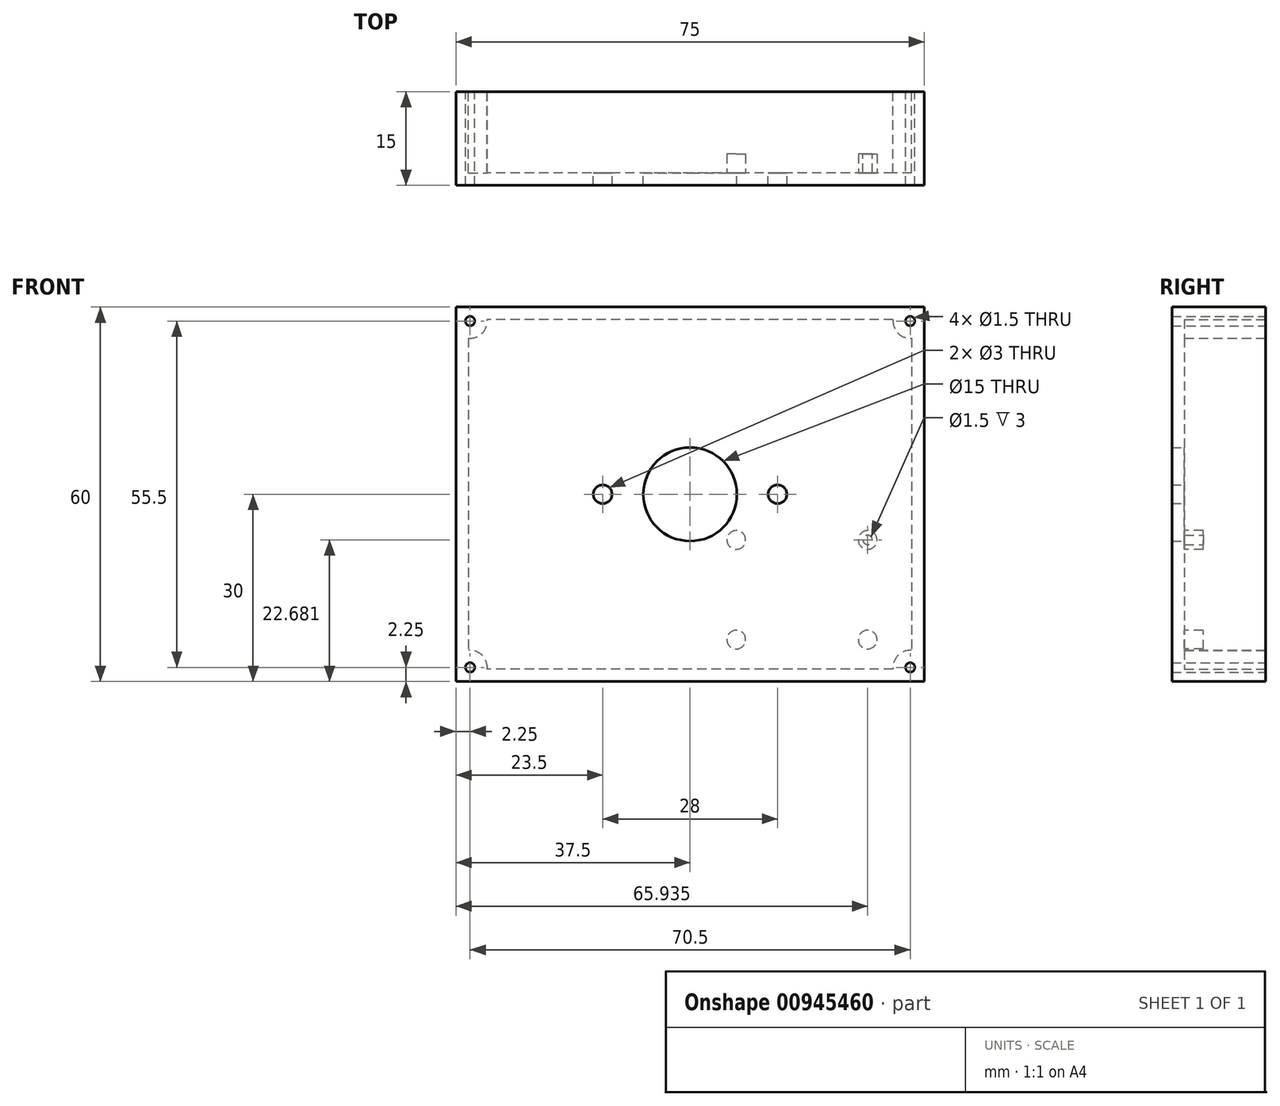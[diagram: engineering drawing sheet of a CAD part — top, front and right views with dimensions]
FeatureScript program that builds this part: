
annotation { "Feature Type Name" : "Feature", "Feature Type Description" : "" }
export const myFeature = defineFeature(function(context is Context, id is Id, definition is map)
    precondition{}
    {
        {
            var Q0;
            Q0=qCreatedBy(makeId("Front.planeOp"),FACE);
            var sketch = newSketch(context, id + "F0", { "sketchPlane" : qUnion([Q0])});
            skLineSegment(sketch, "E0.bottom", {"start": v(37.5, 30) * mm, "end": v(-37.5, 30) * mm});
            skLineSegment(sketch, "E0.top", {"start": v(37.5, -30) * mm, "end": v(-37.5, -30) * mm});
            skLineSegment(sketch, "E0.left", {"start": v(37.5, 30) * mm, "end": v(37.5, -30) * mm});
            skPoint(sketch, "E0.middle", {"position": v(0, 0) * mm});
            skCircle(sketch, "E1", {"center": v(0, 0) * mm, "radius": 7.5 * mm});
            skCircle(sketch, "E2", {"center": v(14, 0) * mm, "radius": 1.5 * mm});
            skCircle(sketch, "E3", {"center": v(-14, 0) * mm, "radius": 1.5 * mm});
            skLineSegment(sketch, "E4.left", {"start": v(-37.5, 30) * mm, "end": v(-37.5, -30) * mm});
            skCircle(sketch, "E5", {"center": v(-35.25, 27.75) * mm, "radius": 0.75 * mm});
            skCircle(sketch, "E6", {"center": v(35.25, 27.75) * mm, "radius": 0.75 * mm});
            skCircle(sketch, "E7", {"center": v(35.25, -27.75) * mm, "radius": 0.75 * mm});
            skCircle(sketch, "E8", {"center": v(-35.25, -27.75) * mm, "radius": 0.75 * mm});
            skSolve(sketch);
        }
        {
            var Q0;
            Q0=qSketchRegion(id+"F0",true);
            var Q1;
            Q1=makeQuery(id+"F0.imprint","IMPRINT",FACE,{"disambiguationData":[TD([[makeQuery(id+"F0.imprint","IMPRINT",EDGE,{"derivedFrom":sQuery(id+"F0.wireOp",EDGE,"E3")}),1.0]])]});
            var Q2;
            Q2=makeQuery(id+"F0.imprint","IMPRINT",FACE,{"disambiguationData":[TD([[makeQuery(id+"F0.imprint","IMPRINT",EDGE,{"derivedFrom":sQuery(id+"F0.wireOp",EDGE,"E1")}),1.0]])]});
            var Q3;
            Q3=makeQuery(id+"F0.imprint","IMPRINT",FACE,{"disambiguationData":[TD([[makeQuery(id+"F0.imprint","IMPRINT",EDGE,{"derivedFrom":sQuery(id+"F0.wireOp",EDGE,"E2")}),1.0]])]});
            extrude(context, id + "F1", {"entities" : qUnion([Q0, Q1, Q2, Q3]), "endBound" : BoundingType.SYMMETRIC, "depth" : 15 * mm, "offsetDistance" : 25.4 * mm});
        }
        {
            var Q0;
            Q0=makeQuery(id+"F1.opExtrude","CAP_FACE",FACE,{"disambiguationData":[OSD([sQuery(id+"F0.wireOp",EDGE,"E0.top"),sQuery(id+"F0.wireOp",EDGE,"E0.left"),sQuery(id+"F0.wireOp",EDGE,"E1"),sQuery(id+"F0.wireOp",EDGE,"E2"),sQuery(id+"F0.wireOp",EDGE,"E3"),sQuery(id+"F0.wireOp",EDGE,"E4.bottom"),sQuery(id+"F0.wireOp",EDGE,"E4.left"),sQuery(id+"F0.wireOp",EDGE,"054ACI62-jY1l-R8Cq-kHqT-064Rme7hxepK.bottom"),sQuery(id+"F0.wireOp",EDGE,"054ACI62-jY1l-R8Cq-kHqT-064Rme7hxepK.right"),sQuery(id+"F0.wireOp",EDGE,"E5"),sQuery(id+"F0.wireOp",EDGE,"E6"),sQuery(id+"F0.wireOp",EDGE,"8eQuBZQc-js6f-clw7-0T8J-KEzLaIp8Z2mv.bottom"),sQuery(id+"F0.wireOp",EDGE,"8eQuBZQc-js6f-clw7-0T8J-KEzLaIp8Z2mv.left"),sQuery(id+"F0.wireOp",EDGE,"E7"),sQuery(id+"F0.wireOp",EDGE,"E8")])],"isStart":true});
            shell(context, id + "F2", {"entities" : qUnion([Q0]), "thickness" : 2 * mm});
        }
        {
            var Q0;
            Q0=makeQuery(id+"F0.imprint","IMPRINT",FACE,{"disambiguationData":[TD([[makeQuery(id+"F0.imprint","IMPRINT",EDGE,{"derivedFrom":sQuery(id+"F0.wireOp",EDGE,"E3")}),1.0]])]});
            var Q1;
            Q1=makeQuery(id+"F0.imprint","IMPRINT",FACE,{"disambiguationData":[TD([[makeQuery(id+"F0.imprint","IMPRINT",EDGE,{"derivedFrom":sQuery(id+"F0.wireOp",EDGE,"E1")}),1.0]])]});
            var Q2;
            Q2=makeQuery(id+"F0.imprint","IMPRINT",FACE,{"disambiguationData":[TD([[makeQuery(id+"F0.imprint","IMPRINT",EDGE,{"derivedFrom":sQuery(id+"F0.wireOp",EDGE,"E2")}),1.0]])]});
            extrude(context, id + "F3", {"entities" : qUnion([Q0, Q1, Q2]), "operationType" : NewBodyOperationType.REMOVE, "endBound" : BoundingType.THROUGH_ALL, "depth" : 25 * mm, "offsetDistance" : 25 * mm});
        }
        {
            var Q0;
            Q0=makeQuery(id+"F2.opShell","OFFSET_FACE",FACE,{"disambiguationData":[OSD([sQuery(id+"F0.wireOp",EDGE,"E0.bottom"),sQuery(id+"F0.wireOp",EDGE,"E0.top"),sQuery(id+"F0.wireOp",EDGE,"E0.left"),sQuery(id+"F0.wireOp",EDGE,"E4.left"),sQuery(id+"F0.wireOp",EDGE,"E5"),sQuery(id+"F0.wireOp",EDGE,"E6"),sQuery(id+"F0.wireOp",EDGE,"E7"),sQuery(id+"F0.wireOp",EDGE,"E8")])]});
            var sketch = newSketch(context, id + "F4", { "sketchPlane" : qUnion([Q0])});
            skLineSegment(sketch, "E9.bottom", {"start": v(-28.43, -7.32) * mm, "end": v(-7.4, -7.32) * mm, "construction": true});
            skLineSegment(sketch, "E9.top", {"start": v(-28.43, -23.29) * mm, "end": v(-7.4, -23.29) * mm, "construction": true});
            skLineSegment(sketch, "E9.left", {"start": v(-28.43, -7.32) * mm, "end": v(-28.43, -23.29) * mm, "construction": true});
            skLineSegment(sketch, "E9.right", {"start": v(-7.4, -7.32) * mm, "end": v(-7.4, -23.29) * mm, "construction": true});
            skCircle(sketch, "E10", {"center": v(-28.43, -7.32) * mm, "radius": 1.5 * mm});
            skCircle(sketch, "E11", {"center": v(-7.4, -7.32) * mm, "radius": 1.5 * mm});
            skCircle(sketch, "E12", {"center": v(-28.43, -23.29) * mm, "radius": 1.5 * mm});
            skCircle(sketch, "E13", {"center": v(-7.4, -23.29) * mm, "radius": 1.5 * mm});
            skSolve(sketch);
        }
        {
            var Q0;
            Q0=makeQuery(id+"F4.imprint","IMPRINT",FACE,{"disambiguationData":[TD([[makeQuery(id+"F4.imprint","IMPRINT",EDGE,{"derivedFrom":sQuery(id+"F4.wireOp",EDGE,"E10")}),1.0]])]});
            var Q1;
            Q1=makeQuery(id+"F4.imprint","IMPRINT",FACE,{"disambiguationData":[TD([[makeQuery(id+"F4.imprint","IMPRINT",EDGE,{"derivedFrom":sQuery(id+"F4.wireOp",EDGE,"E11")}),1.0]])]});
            var Q2;
            Q2=makeQuery(id+"F4.imprint","IMPRINT",FACE,{"disambiguationData":[TD([[makeQuery(id+"F4.imprint","IMPRINT",EDGE,{"derivedFrom":sQuery(id+"F4.wireOp",EDGE,"E12")}),1.0]])]});
            var Q3;
            Q3=makeQuery(id+"F4.imprint","IMPRINT",FACE,{"disambiguationData":[TD([[makeQuery(id+"F4.imprint","IMPRINT",EDGE,{"derivedFrom":sQuery(id+"F4.wireOp",EDGE,"E13")}),1.0]])]});
            extrude(context, id + "F5", {"entities" : qUnion([Q0, Q1, Q2, Q3]), "operationType" : NewBodyOperationType.ADD, "depth" : 3 * mm, "offsetDistance" : 25 * mm});
        }
        {
            var Q0;
            Q0=makeQuery(id+"F5.opExtrude","CAP_FACE",FACE,{"disambiguationData":[OSD([sQuery(id+"F4.wireOp",EDGE,"E10")])],"isStart":false});
            var sketch = newSketch(context, id + "F6", { "sketchPlane" : qUnion([Q0])});
            skCircle(sketch, "E14.0.0", {"center": v(-28.43, -7.32) * mm, "radius": 1.5 * mm});
            skCircle(sketch, "E15.0.0", {"center": v(-7.4, -7.32) * mm, "radius": 1.5 * mm});
            skCircle(sketch, "E16.0.0", {"center": v(-7.4, -23.29) * mm, "radius": 1.5 * mm});
            skCircle(sketch, "E17.0.0", {"center": v(-28.43, -23.29) * mm, "radius": 1.5 * mm});
            skCircle(sketch, "E18", {"center": v(-28.43, -7.32) * mm, "radius": 0.75 * mm});
            skSolve(sketch);
        }
        {
            var Q0;
            Q0=makeQuery(id+"F6.imprint","IMPRINT",FACE,{"disambiguationData":[TD([[makeQuery(id+"F6.imprint","IMPRINT",EDGE,{"derivedFrom":sQuery(id+"F6.wireOp",EDGE,"E18")}),1.0]])]});
            extrude(context, id + "F7", {"entities" : qUnion([Q0]), "operationType" : NewBodyOperationType.REMOVE, "oppositeDirection" : true, "depth" : 3 * mm, "offsetDistance" : 25 * mm});
        }
    });
